# Revit family: Sink-Under_Mount-Lavatory-KOHLER-Verticyl-K-8188
name_source: partatom
category: Plumbing Fixtures
revit_build: Autodesk Revit 2017 (Build: 20160225_1515(x64)
units: mm (PartAtom-declared; Revit-internal decimal feet)

## family parameters
Cut with Voids When Loaded = No
Host = Face
OmniClass Number = 23.31.13.00
OmniClass Title = Sinks
Part Type = Normal
Room Calculation Point = No
Round Connector Dimension = Use Diameter
Shared = No

## types (6) — shared parameters
ADA Compliant = Yes
Assembly Code = D2010400
CW Connection = No
Cold Water Inlet = Cold Water Inlet
Date Modified = 04/08/2020
Default Elevation = 34"
Description = Undermount bathroom sink
Drain Included = No
HW Connection = No
Height = 7 3/16"
Hot Water Inlet = Hot Water Inlet
Length = 13 1/16"
Manufacturer = KOHLER Co.
MasterFormat 1995 = 15410
MasterFormat 2004 = 22.41.16
Material = Vitreous China
Product Documentation Link = https://www.us.kohler.com
Product Name = Verticyl
Product Page URL = http://www.us.kohler.com
URL = https://www.us.kohler.com
Vent Connection = No
Waste Connection = Yes
Waste Water Outlet = Waste Water Outlet
WaterSense Certified = No
Width = 13 1/4"

## per-type parameters (varying)
| type | Finish | Model | Type |
| 7-Black Black | Kohler-Vitreous_China-7-Black_Black | K-8188-7 | 6 |
| 58-Thunder Grey | Kohler-Vitreous_China-58-Thunder_Grey | K-8188-58 | 5 |
| 95-Ice Grey | Kohler-Vitreous_China-95-Ice_Grey | K-8188-95 | 4 |
| NY-Dune | Kohler-Vitreous_China-NY-Dune | K-8188-NY | 3 |
| 96-Biscuit | Kohler-Vitreous_China-96-Biscuit | K-8188-96 | 2 |
| 0-White | Kohler-Vitreous_China-0-White | K-8188-0 | 1 |

## geometry (parser evidence)
native form markers: Sweep x4
no freeform markers — native parametric forms only
